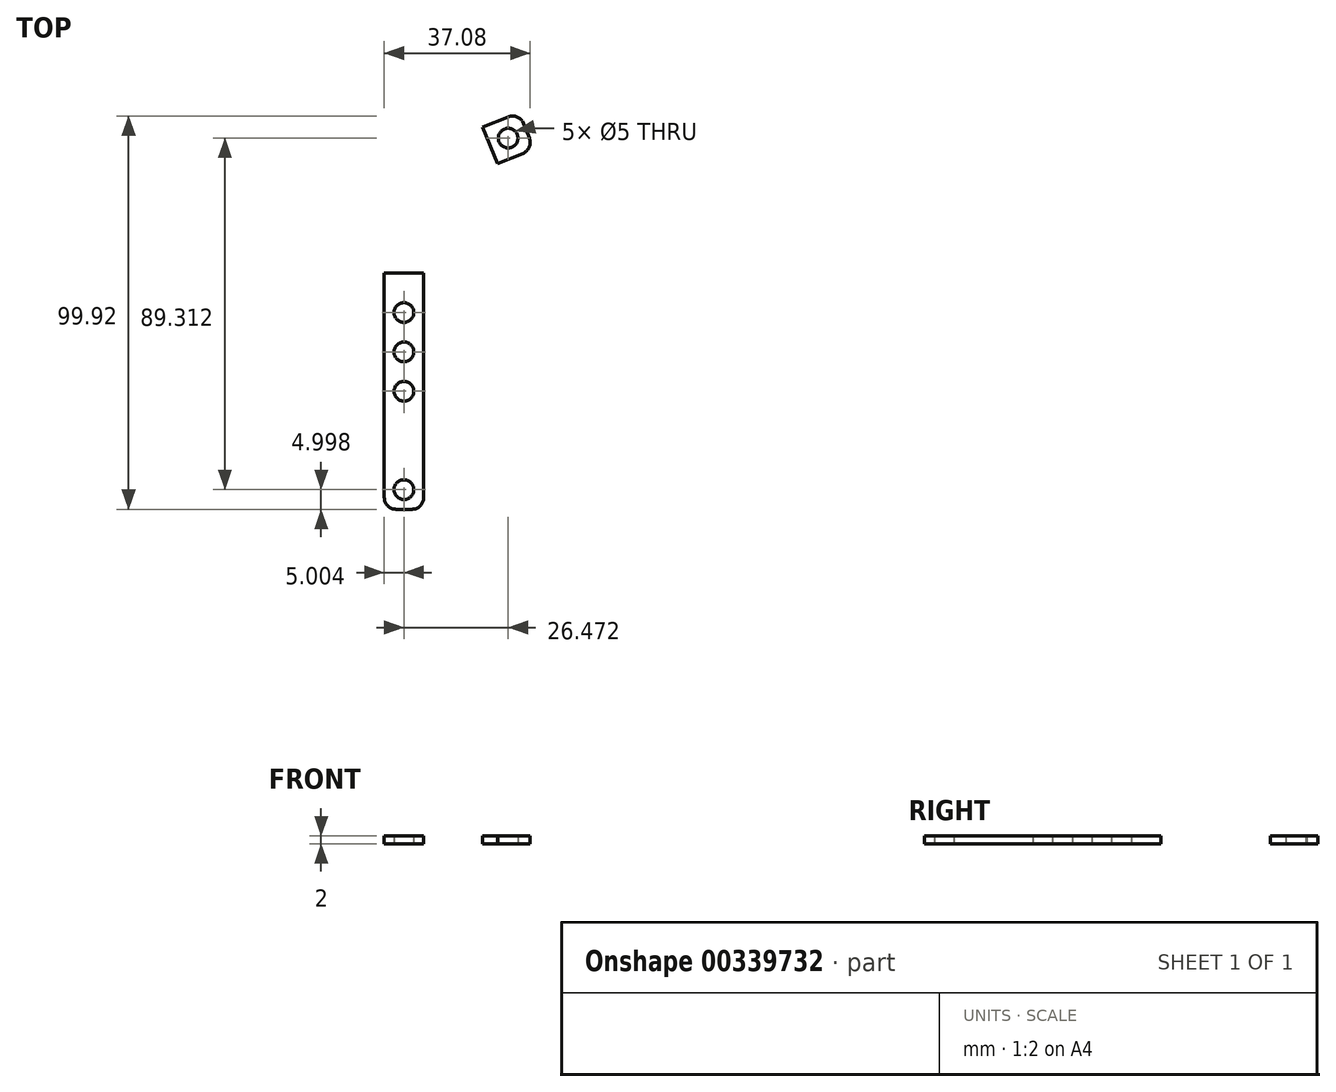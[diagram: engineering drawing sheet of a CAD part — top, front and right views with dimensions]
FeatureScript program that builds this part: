
annotation { "Feature Type Name" : "Feature", "Feature Type Description" : "" }
export const myFeature = defineFeature(function(context is Context, id is Id, definition is map)
    precondition{}
    {
        {
            var Q0;
            Q0=qCreatedBy(makeId("Top.planeOp"),FACE);
            var sketch = newSketch(context, id + "F0", { "sketchPlane" : qUnion([Q0])});
            skLineSegment(sketch, "E0", {"start": v(-19.93, 7.5) * mm, "end": v(-9.93, 7.5) * mm});
            skLineSegment(sketch, "E1", {"start": v(-19.93, 7.5) * mm, "end": v(-19.93, 67.5) * mm});
            skLineSegment(sketch, "E2", {"start": v(-9.93, 7.5) * mm, "end": v(-9.93, 67.5) * mm});
            skPoint(sketch, "E3", {"position": v(20.07, 67.5) * mm});
            skArc(sketch, "E4", {"start": v(-19.93, 67.5) * mm, "mid": v(-13.1, 89.85) * mm, "end": v(5.03, 104.57) * mm});
            skLineSegment(sketch, "E5", {"start": v(5.03, 104.57) * mm, "end": v(8.8, 95.3) * mm});
            skArc(sketch, "E6", {"start": v(-9.93, 67.5) * mm, "mid": v(-4.81, 84.27) * mm, "end": v(8.8, 95.3) * mm});
            skLineSegment(sketch, "E7", {"start": v(-19.93, 67.5) * mm, "end": v(-9.93, 67.5) * mm});
            skArc(sketch, "E8", {"start": v(-14.93, 67.5) * mm, "mid": v(-8.96, 87.06) * mm, "end": v(6.91, 99.94) * mm});
            skLineSegment(sketch, "E9", {"start": v(5.03, 104.57) * mm, "end": v(14.3, 108.33) * mm});
            skLineSegment(sketch, "E10", {"start": v(14.3, 108.33) * mm, "end": v(18.06, 99.07) * mm});
            skLineSegment(sketch, "E11", {"start": v(8.8, 95.3) * mm, "end": v(18.06, 99.07) * mm});
            skLineSegment(sketch, "E12", {"start": v(14.3, 108.33) * mm, "end": v(8.8, 95.3) * mm});
            skLineSegment(sketch, "E13", {"start": v(5.03, 104.57) * mm, "end": v(18.06, 99.07) * mm});
            skPoint(sketch, "E14", {"position": v(11.55, 101.82) * mm});
            skCircle(sketch, "E15", {"center": v(11.55, 101.82) * mm, "radius": 2.5 * mm});
            skLineSegment(sketch, "E16", {"start": v(-14.93, 67.5) * mm, "end": v(-14.93, 7.5) * mm});
            skCircle(sketch, "E17", {"center": v(-14.93, 57.5) * mm, "radius": 2.5 * mm});
            skCircle(sketch, "E18", {"center": v(-14.93, 47.5) * mm, "radius": 2.5 * mm});
            skCircle(sketch, "E19", {"center": v(-14.93, 37.5) * mm, "radius": 2.5 * mm});
            skCircle(sketch, "E20", {"center": v(-14.93, 12.5) * mm, "radius": 2.5 * mm});
            skSolve(sketch);
        }
        {
            var Q0;
            Q0=makeQuery(id+"F0.imprint","IMPRINT",FACE,{"disambiguationData":[TD([[makeQuery(id+"F0.imprint","IMPRINT",EDGE,{"derivedFrom":sQuery(id+"F0.wireOp",EDGE,"E0")}),1.0]])]});
            var Q1;
            {var subQ0=sQuery(id+"F0.wireOp",EDGE,"E4");Q1=makeQuery(id+"F0.imprint","IMPRINT",FACE,{"disambiguationData":[TD([[makeQuery(id+"F0.imprint","IMPRINT",EDGE,{"derivedFrom":subQ0}),-1.0]])]});}
            var Q2;
            {var subQ0=sQuery(id+"F0.wireOp",EDGE,"E6");Q2=makeQuery(id+"F0.imprint","IMPRINT",FACE,{"disambiguationData":[TD([[makeQuery(id+"F0.imprint","IMPRINT",EDGE,{"derivedFrom":subQ0}),1.0]])]});}
            var Q3;
            {var subQ3=sQuery(id+"F0.wireOp",EDGE,"E15");var subQ5=sQuery(id+"F0.wireOp",EDGE,"E12");var subQ7=makeQuery(id+"F0.imprint","INTERSECT",VERTEX,{"disambiguationData":[OD(1.0)],"derivedFrom":[subQ5,subQ3]});Q3=makeQuery(id+"F0.imprint","IMPRINT",FACE,{"disambiguationData":[TD([[makeQuery(id+"F0.imprint","IMPRINT",EDGE,{"disambiguationData":[TD([[subQ7,1.0]])],"derivedFrom":subQ3}),-1.0]])]});}
            var Q4;
            {var subQ0=sQuery(id+"F0.wireOp",EDGE,"E11");Q4=makeQuery(id+"F0.imprint","IMPRINT",FACE,{"disambiguationData":[TD([[makeQuery(id+"F0.imprint","IMPRINT",EDGE,{"derivedFrom":subQ0}),1.0]])]});}
            var Q5;
            {var subQ0=sQuery(id+"F0.wireOp",EDGE,"E10");Q5=makeQuery(id+"F0.imprint","IMPRINT",FACE,{"disambiguationData":[TD([[makeQuery(id+"F0.imprint","IMPRINT",EDGE,{"derivedFrom":subQ0}),-1.0]])]});}
            var Q6;
            {var subQ0=sQuery(id+"F0.wireOp",EDGE,"E9");Q6=makeQuery(id+"F0.imprint","IMPRINT",FACE,{"disambiguationData":[TD([[makeQuery(id+"F0.imprint","IMPRINT",EDGE,{"derivedFrom":subQ0}),-1.0]])]});}
            extrude(context, id + "F1", {"entities" : qUnion([Q0, Q1, Q2, Q3, Q4, Q5, Q6]), "depth" : 2 * mm});
        }
        {
            var Q0;
            Q0=makeQuery(id+"F1.opExtrude","SWEPT_EDGE",EDGE,{"disambiguationData":[OSD([sQuery(id+"F0.wireOp",EDGE,"E9"),sQuery(id+"F0.wireOp",EDGE,"E10"),sQuery(id+"F0.wireOp",EDGE,"E12")])]});
            var Q1;
            Q1=makeQuery(id+"F1.opExtrude","SWEPT_EDGE",EDGE,{"disambiguationData":[OSD([sQuery(id+"F0.wireOp",EDGE,"E10"),sQuery(id+"F0.wireOp",EDGE,"E11"),sQuery(id+"F0.wireOp",EDGE,"E13")])]});
            var Q2;
            Q2=makeQuery(id+"F1.opExtrude","SWEPT_EDGE",EDGE,{"disambiguationData":[OSD([sQuery(id+"F0.wireOp",EDGE,"E0"),sQuery(id+"F0.wireOp",EDGE,"E2")])]});
            var Q3;
            Q3=makeQuery(id+"F1.opExtrude","SWEPT_EDGE",EDGE,{"disambiguationData":[OSD([sQuery(id+"F0.wireOp",EDGE,"E0"),sQuery(id+"F0.wireOp",EDGE,"E1")])]});
            fillet(context, id + "F2", {"entities" : qUnion([Q0, Q1, Q2, Q3]), "radius" : 3 * mm, "tangentPropagation" : true, "allowEdgeOverflow" : false});
        }
    });
